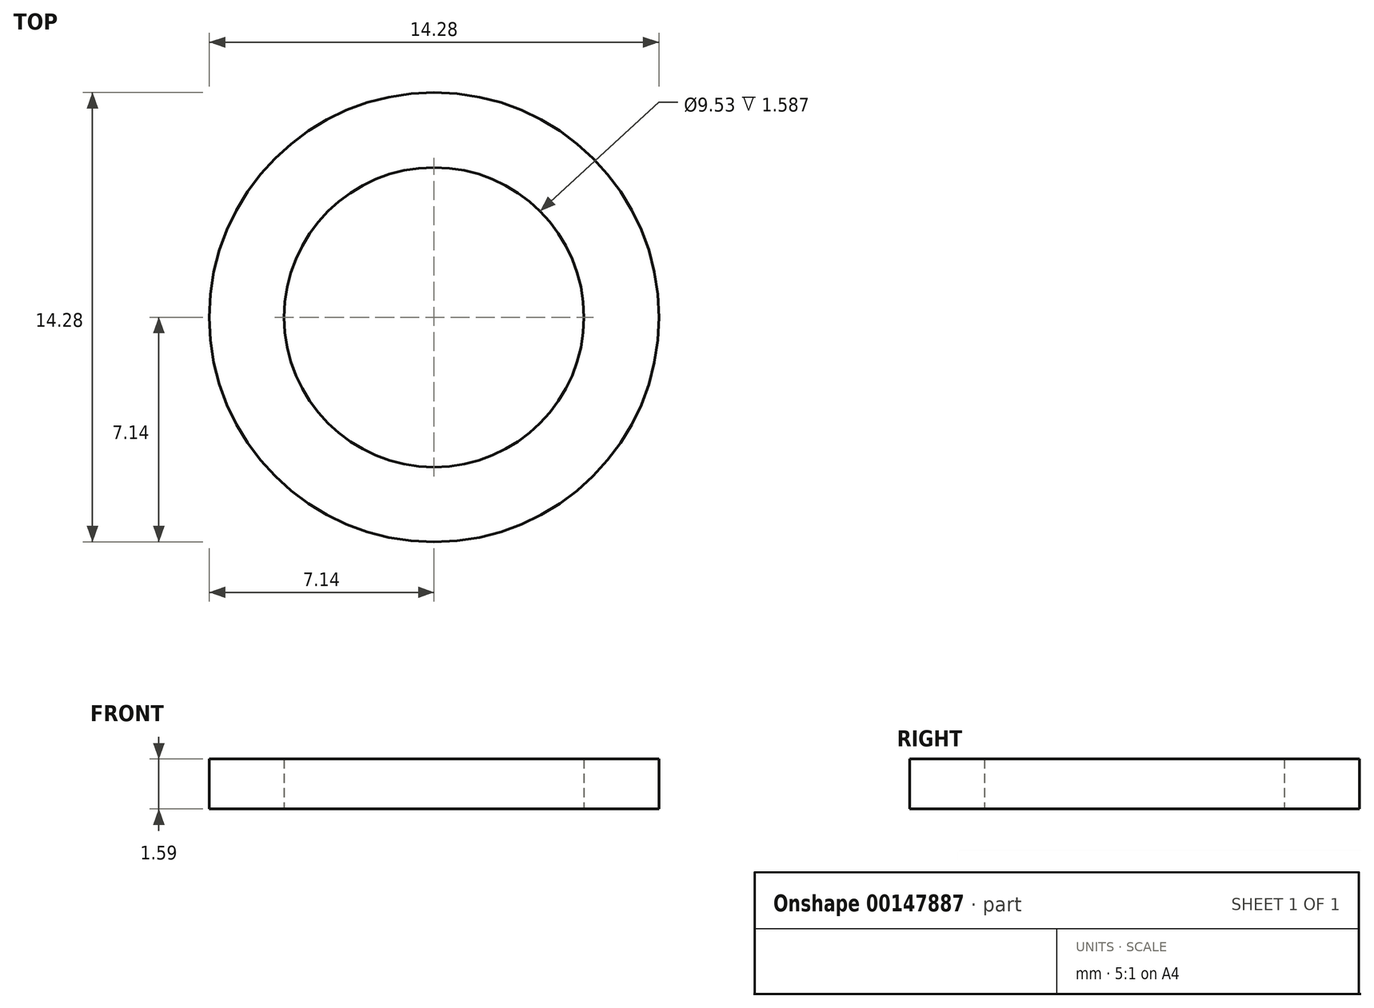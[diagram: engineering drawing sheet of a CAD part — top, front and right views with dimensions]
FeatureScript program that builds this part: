
annotation { "Feature Type Name" : "Feature", "Feature Type Description" : "" }
export const myFeature = defineFeature(function(context is Context, id is Id, definition is map)
    precondition{}
    {
        {
            var Q0;
            Q0=qCreatedBy(makeId("Top.planeOp"),FACE);
            var sketch = newSketch(context, id + "F0", { "sketchPlane" : qUnion([Q0])});
            skCircle(sketch, "E0", {"center": v(0, 0) * mm, "radius": 4.76 * mm});
            skCircle(sketch, "E1", {"center": v(0, 0) * mm, "radius": 7.14 * mm});
            skSolve(sketch);
        }
        {
            var Q0;
            Q0=qSketchRegion(id+"F0",true);
            extrude(context, id + "F1", {"entities" : qUnion([Q0]), "depth" : 1.59 * mm});
        }
    });
